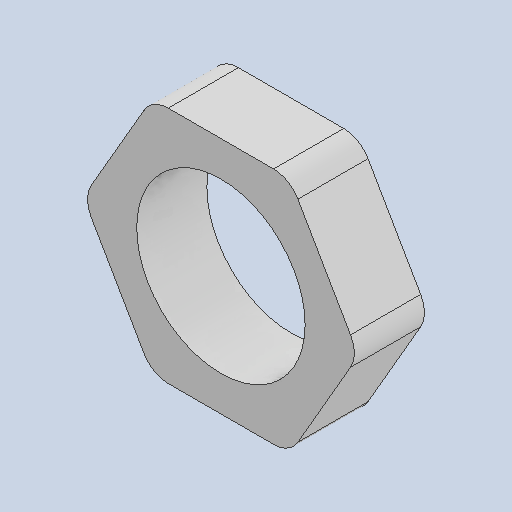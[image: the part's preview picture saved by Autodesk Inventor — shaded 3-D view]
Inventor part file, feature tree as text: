
AUTODESK INVENTOR PART (.ipt)
format: ipt  version: 2024.2 (Build 282272000, 272)  size: 119,808 bytes
history: native  units: mm
features: extrude x2, fillet x1, sketch x1
ambient origin geometry x8: Origin, YZ Plane, XZ Plane, XY Plane, X Axis, Y Axis, Z Axis, Center Point
bodies: Solid1 (feature_tree)
feature tree (4):
  extrude  "Extrusion1"  Depth=5.0mm TaperAngle=0.0deg
  extrude  "Extrusion2"  Depth=2.0mm
  fillet  "Fillet1"  [1 undecoded]
  sketch  "Sketch1"  dims[d0=17.0mm d1=5.0mm d2=0.0mm d3=12.0mm d4=0.0mm d5=0.0mm d6=2.0mm]
note: 1 required parameter value undecoded (feature->parameter linkage not recoverable at this tier; creation-order binding heuristic only, values carry confidence <= 0.55)
